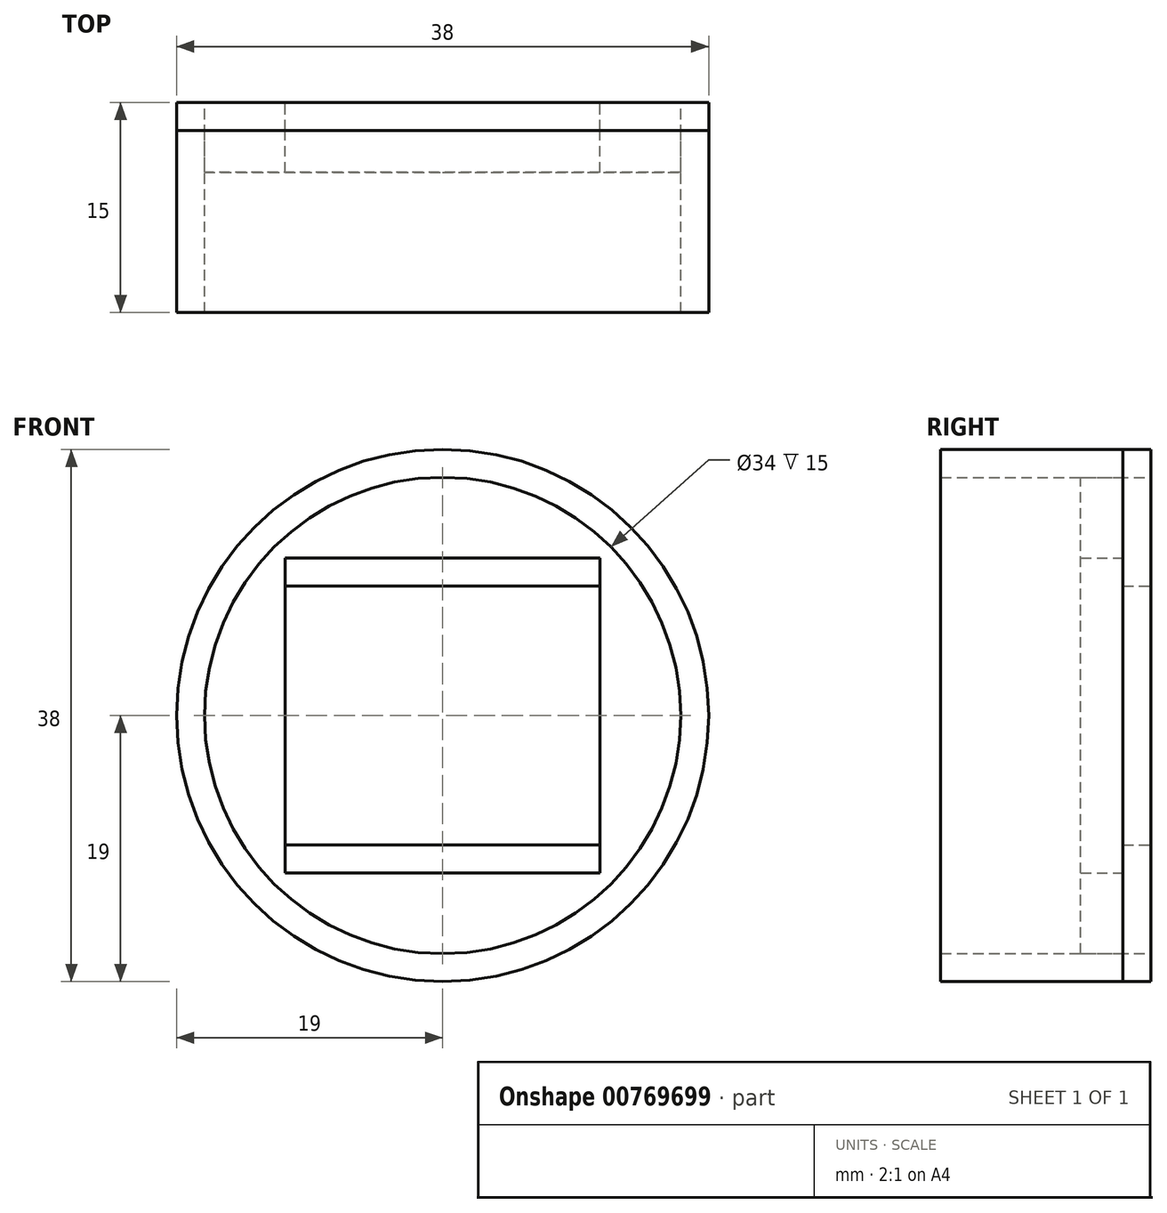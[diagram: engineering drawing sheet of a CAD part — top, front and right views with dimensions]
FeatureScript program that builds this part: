
annotation { "Feature Type Name" : "Feature", "Feature Type Description" : "" }
export const myFeature = defineFeature(function(context is Context, id is Id, definition is map)
    precondition{}
    {
        {
            var Q0;
            Q0=qCreatedBy(makeId("Front.planeOp"),FACE);
            var sketch = newSketch(context, id + "F0", { "sketchPlane" : qUnion([Q0])});
            skLineSegment(sketch, "E0.bottom", {"start": v(11.25, -11.25) * mm, "end": v(-11.25, -11.25) * mm});
            skLineSegment(sketch, "E0.top", {"start": v(11.25, 11.25) * mm, "end": v(-11.25, 11.25) * mm});
            skLineSegment(sketch, "E0.left", {"start": v(11.25, -11.25) * mm, "end": v(11.25, 11.25) * mm});
            skLineSegment(sketch, "E0.right", {"start": v(-11.25, -11.25) * mm, "end": v(-11.25, 11.25) * mm});
            skPoint(sketch, "E0.middle", {"position": v(0, 0) * mm});
            skCircle(sketch, "E1", {"center": v(0, 0) * mm, "radius": 19 * mm});
            skCircle(sketch, "E2", {"center": v(0, 0) * mm, "radius": 17 * mm});
            skLineSegment(sketch, "E3.bottom", {"start": v(-11.25, 11.25) * mm, "end": v(11.25, 11.25) * mm});
            skLineSegment(sketch, "E3.top", {"start": v(-11.25, 9.25) * mm, "end": v(11.25, 9.25) * mm});
            skLineSegment(sketch, "E3.left", {"start": v(-11.25, 11.25) * mm, "end": v(-11.25, 9.25) * mm});
            skLineSegment(sketch, "E3.right", {"start": v(11.25, 11.25) * mm, "end": v(11.25, 9.25) * mm});
            skLineSegment(sketch, "E4.bottom", {"start": v(-11.25, -9.25) * mm, "end": v(11.25, -9.25) * mm});
            skLineSegment(sketch, "E4.top", {"start": v(-11.25, -11.25) * mm, "end": v(11.25, -11.25) * mm});
            skLineSegment(sketch, "E4.left", {"start": v(-11.25, -9.25) * mm, "end": v(-11.25, -11.25) * mm});
            skLineSegment(sketch, "E4.right", {"start": v(11.25, -9.25) * mm, "end": v(11.25, -11.25) * mm});
            skSolve(sketch);
        }
        {
            var Q0;
            {var subQ6=sQuery(id+"F0.wireOp",EDGE,"E0.bottom");Q0=makeQuery(id+"F0.imprint","IMPRINT",FACE,{"disambiguationData":[TD([[makeQuery(id+"F0.imprint","IMPRINT",EDGE,{"derivedFrom":subQ6}),1.0]])]});}
            extrude(context, id + "F1", {"entities" : qUnion([Q0]), "depth" : 5 * mm, "offsetDistance" : 25 * mm});
        }
        {
            var Q0;
            {var subQ0=sQuery(id+"F0.wireOp",EDGE,"E0.top");Q0=makeQuery(id+"F0.imprint","IMPRINT",FACE,{"disambiguationData":[TD([[makeQuery(id+"F0.imprint","IMPRINT",EDGE,{"derivedFrom":subQ0}),1.0]])]});}
            var Q1;
            {var subQ0=sQuery(id+"F0.wireOp",EDGE,"E0.bottom");Q1=makeQuery(id+"F0.imprint","IMPRINT",FACE,{"disambiguationData":[TD([[makeQuery(id+"F0.imprint","IMPRINT",EDGE,{"derivedFrom":subQ0}),-1.0]])]});}
            var Q2;
            {var subQ6=sQuery(id+"F0.wireOp",EDGE,"E0.bottom");Q2=makeQuery(id+"F0.imprint","IMPRINT",FACE,{"disambiguationData":[TD([[makeQuery(id+"F0.imprint","IMPRINT",EDGE,{"derivedFrom":subQ6}),1.0]])]});}
            var Q3;
            Q3=makeQuery(id+"F0.imprint","IMPRINT",FACE,{"disambiguationData":[TD([[makeQuery(id+"F0.imprint","IMPRINT",EDGE,{"derivedFrom":sQuery(id+"F0.wireOp",EDGE,"E1")}),1.0]])]});
            extrude(context, id + "F2", {"entities" : qUnion([Q0, Q1, Q2, Q3]), "operationType" : NewBodyOperationType.ADD, "depth" : 2 * mm, "offsetDistance" : 25 * mm});
        }
        {
            var Q0;
            {var subQ0=sQuery(id+"F0.wireOp",EDGE,"E0.bottom");Q0=makeQuery(id+"F0.imprint","IMPRINT",FACE,{"disambiguationData":[TD([[makeQuery(id+"F0.imprint","IMPRINT",EDGE,{"derivedFrom":subQ0}),-1.0]])]});}
            extrude(context, id + "F3", {"entities" : qUnion([Q0]), "operationType" : NewBodyOperationType.ADD, "depth" : 2 * mm, "offsetDistance" : 25 * mm});
        }
        {
            var Q0;
            Q0=makeQuery(id+"F0.imprint","IMPRINT",FACE,{"disambiguationData":[TD([[makeQuery(id+"F0.imprint","IMPRINT",EDGE,{"derivedFrom":sQuery(id+"F0.wireOp",EDGE,"E1")}),1.0]])]});
            var Q1;
            Q1=sQuery(id+"F0.wireOp",EDGE,"E1");
            var Q2;
            Q2=sQuery(id+"F0.wireOp",EDGE,"E2");
            extrude(context, id + "F4", {"entities" : qUnion([Q0]), "surfaceEntities" : qUnion([Q1, Q2]), "depth" : 15 * mm, "offsetDistance" : 25 * mm});
        }
    });
